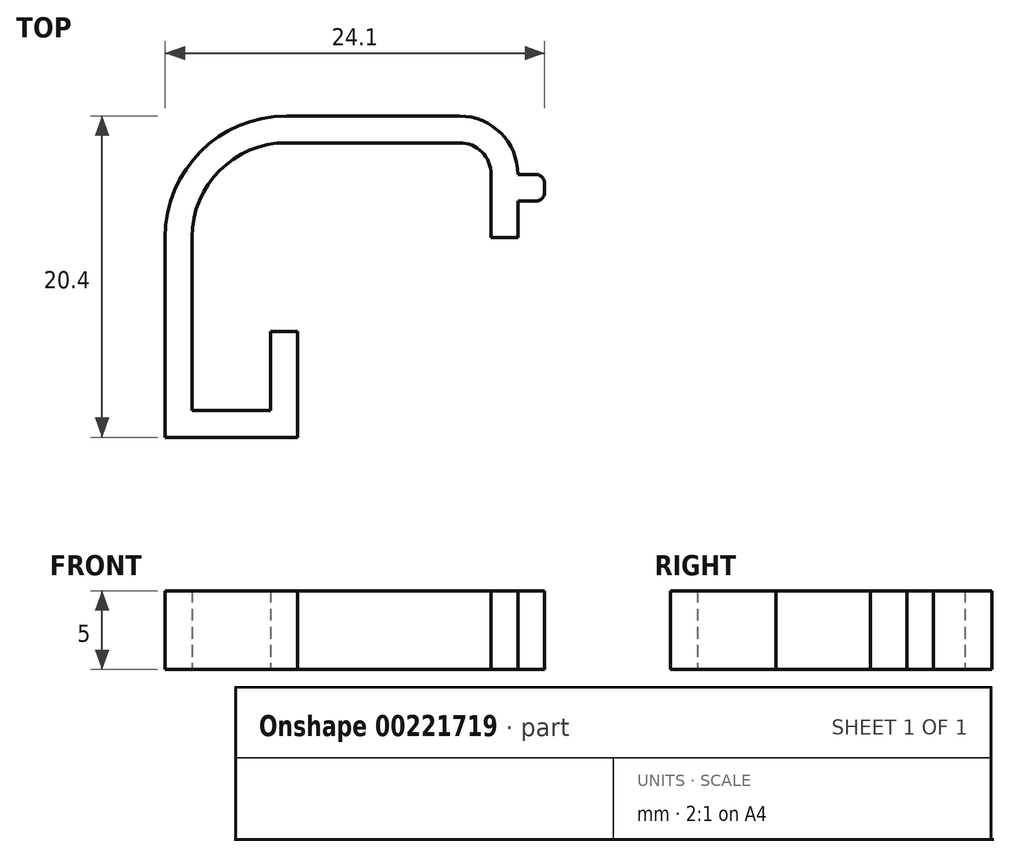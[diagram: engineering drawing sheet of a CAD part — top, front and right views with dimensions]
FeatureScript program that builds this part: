
annotation { "Feature Type Name" : "Feature", "Feature Type Description" : "" }
export const myFeature = defineFeature(function(context is Context, id is Id, definition is map)
    precondition{}
    {
        {
            var Q0;
            Q0=qCreatedBy(makeId("Top.planeOp"),FACE);
            var sketch = newSketch(context, id + "F0", { "sketchPlane" : qUnion([Q0])});
            skLineSegment(sketch, "E0", {"start": v(0, 0) * mm, "end": v(5, 0) * mm});
            skLineSegment(sketch, "E1", {"start": v(5, 0) * mm, "end": v(5, 5) * mm});
            skLineSegment(sketch, "E2", {"start": v(5, 5) * mm, "end": v(6.7, 5) * mm});
            skLineSegment(sketch, "E3", {"start": v(6.7, 5) * mm, "end": v(6.7, -1.7) * mm});
            skLineSegment(sketch, "E4", {"start": v(6.7, -1.7) * mm, "end": v(-1.7, -1.7) * mm});
            skLineSegment(sketch, "E5", {"start": v(-1.7, -1.7) * mm, "end": v(-1.7, 11) * mm});
            skLineSegment(sketch, "E6", {"start": v(0, 0) * mm, "end": v(0, 11) * mm});
            skArc(sketch, "E7", {"start": v(6, 17) * mm, "mid": v(1.76, 15.24) * mm, "end": v(0, 11) * mm});
            skArc(sketch, "E8", {"start": v(6, 18.7) * mm, "mid": v(0.56, 16.44) * mm, "end": v(-1.7, 11) * mm});
            skLineSegment(sketch, "E9", {"start": v(6, 18.7) * mm, "end": v(17, 18.7) * mm});
            skLineSegment(sketch, "E10", {"start": v(6, 17) * mm, "end": v(17, 17) * mm});
            skArc(sketch, "E11", {"start": v(17, 17) * mm, "mid": v(18.41, 16.41) * mm, "end": v(19, 15) * mm});
            skArc(sketch, "E12", {"start": v(17, 18.7) * mm, "mid": v(19.62, 17.62) * mm, "end": v(20.7, 15) * mm});
            skLineSegment(sketch, "E13", {"start": v(19, 15) * mm, "end": v(19, 11) * mm});
            skLineSegment(sketch, "E14", {"start": v(19, 11) * mm, "end": v(20.7, 11) * mm});
            skLineSegment(sketch, "E15", {"start": v(20.7, 15) * mm, "end": v(21.83, 15) * mm});
            skLineSegment(sketch, "E16", {"start": v(22.4, 14.43) * mm, "end": v(22.4, 13.87) * mm});
            skLineSegment(sketch, "E17", {"start": v(21.83, 13.3) * mm, "end": v(20.7, 13.3) * mm});
            skLineSegment(sketch, "E18", {"start": v(20.7, 13.3) * mm, "end": v(20.7, 11) * mm});
            skPoint(sketch, "E19.visualSharp", {"position": v(22.4, 15) * mm});
            skArc(sketch, "E19.filletArc", {"start": v(22.4, 14.43) * mm, "mid": v(22.23, 14.83) * mm, "end": v(21.83, 15) * mm});
            skPoint(sketch, "E20.visualSharp", {"position": v(22.4, 13.3) * mm});
            skArc(sketch, "E20.filletArc", {"start": v(21.83, 13.3) * mm, "mid": v(22.23, 13.47) * mm, "end": v(22.4, 13.87) * mm});
            skSolve(sketch);
        }
        {
            var Q0;
            Q0=makeQuery(id+"F0.imprint","IMPRINT",FACE,{"disambiguationData":[TD([[makeQuery(id+"F0.imprint","IMPRINT",EDGE,{"derivedFrom":sQuery(id+"F0.wireOp",EDGE,"E0")}),-1.0]])]});
            extrude(context, id + "F1", {"entities" : qUnion([Q0]), "depth" : 5 * mm});
        }
    });
